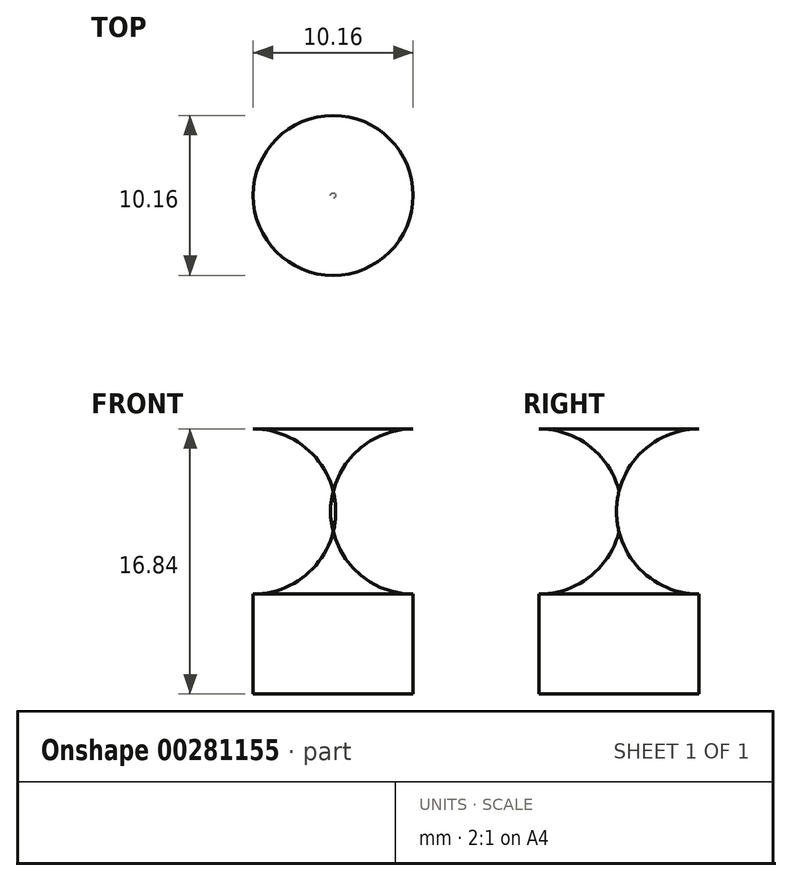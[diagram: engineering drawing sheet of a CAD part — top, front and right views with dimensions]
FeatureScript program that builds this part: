
annotation { "Feature Type Name" : "Feature", "Feature Type Description" : "" }
export const myFeature = defineFeature(function(context is Context, id is Id, definition is map)
    precondition{}
    {
        {
            var Q0;
            Q0=qCreatedBy(makeId("Front.planeOp"),FACE);
            var sketch = newSketch(context, id + "F0", { "sketchPlane" : qUnion([Q0])});
            skLineSegment(sketch, "E0", {"start": v(0, 0) * mm, "end": v(5.08, 0) * mm});
            skLineSegment(sketch, "E1", {"start": v(5.08, 0) * mm, "end": v(5.08, 6.35) * mm});
            skLineSegment(sketch, "E2", {"start": v(5.08, 16.84) * mm, "end": v(0, 16.84) * mm});
            skArc(sketch, "E3", {"start": v(5.08, 6.35) * mm, "mid": v(10.32, 11.6) * mm, "end": v(5.08, 16.84) * mm});
            skLineSegment(sketch, "E4", {"start": v(0, 16.84) * mm, "end": v(0, 0) * mm});
            skSolve(sketch);
        }
        {
            var Q0;
            Q0 = qSketchRegion(id + "F0", true);
            var Q1;
            Q1=sQuery(id+"F0.wireOp",EDGE,"E4");
            revolve(context, id + "F1", {"entities" : qUnion([Q0]), "axis" : qUnion([Q1]), "revolveType" : RevolveType.FULL});
        }
    });
